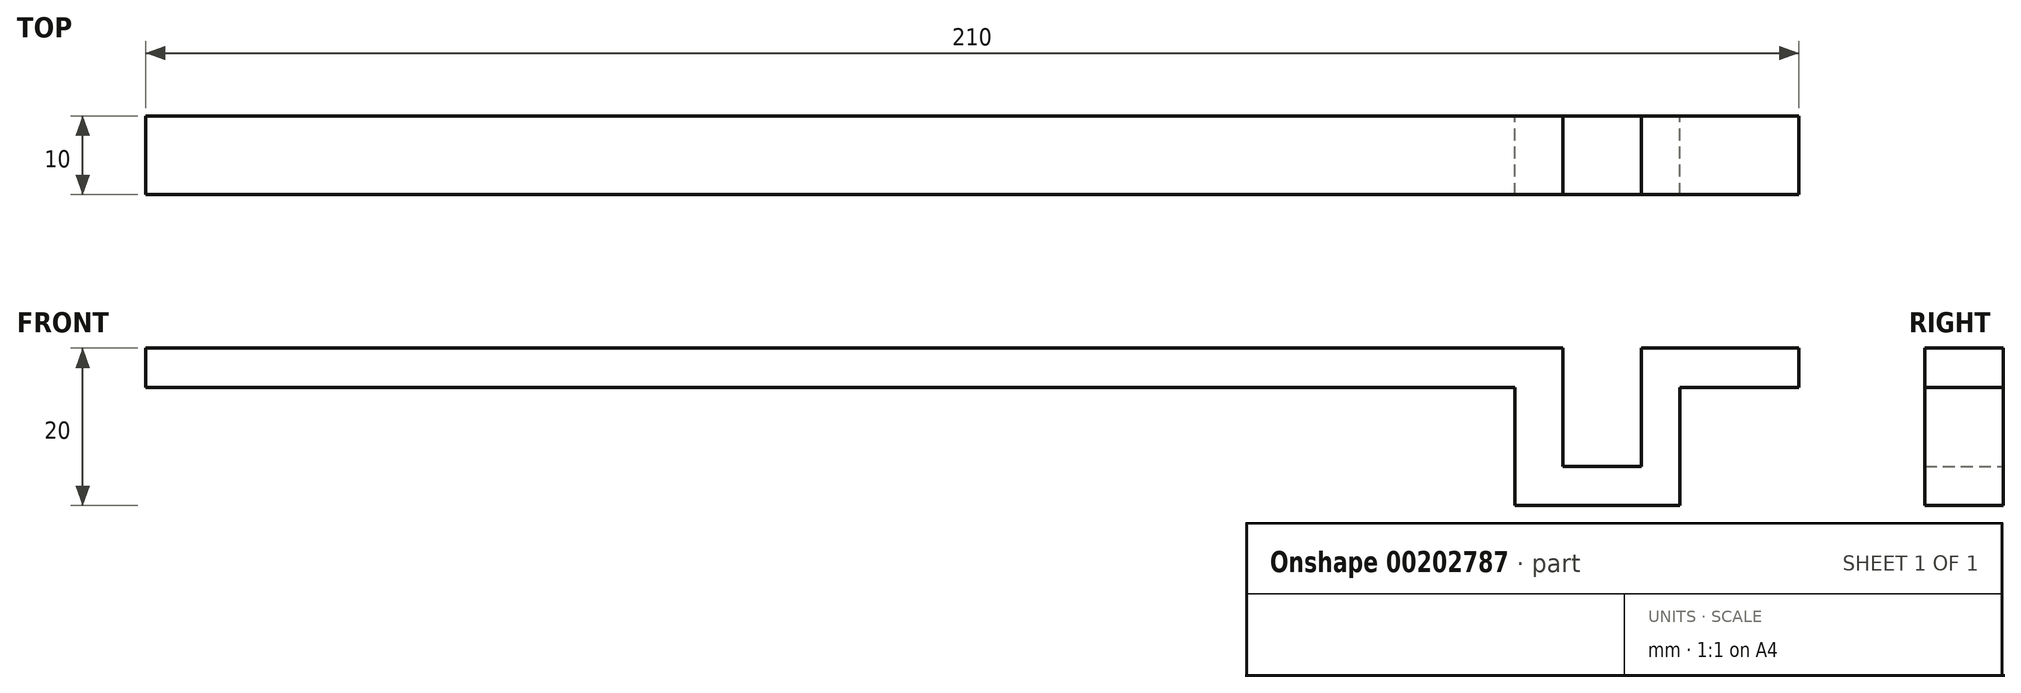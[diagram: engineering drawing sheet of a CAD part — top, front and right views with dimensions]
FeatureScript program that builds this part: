
annotation { "Feature Type Name" : "Feature", "Feature Type Description" : "" }
export const myFeature = defineFeature(function(context is Context, id is Id, definition is map)
    precondition{}
    {
        {
            var Q0;
            Q0=qCreatedBy(makeId("Front.planeOp"),FACE);
            var sketch = newSketch(context, id + "F0", { "sketchPlane" : qUnion([Q0])});
            skLineSegment(sketch, "E0", {"start": v(0, 0) * mm, "end": v(180, 0) * mm});
            skLineSegment(sketch, "E1", {"start": v(180, 0) * mm, "end": v(180, -15) * mm});
            skLineSegment(sketch, "E2", {"start": v(180, -15) * mm, "end": v(190, -15) * mm});
            skLineSegment(sketch, "E3", {"start": v(190, -15) * mm, "end": v(190, 0) * mm});
            skLineSegment(sketch, "E4", {"start": v(190, 0) * mm, "end": v(210, 0) * mm});
            skLineSegment(sketch, "E5", {"start": v(0, 0) * mm, "end": v(0, -5) * mm});
            skLineSegment(sketch, "E6", {"start": v(0, -5) * mm, "end": v(173.92, -5) * mm});
            skLineSegment(sketch, "E7", {"start": v(173.92, -5) * mm, "end": v(173.92, -20) * mm});
            skLineSegment(sketch, "E8", {"start": v(173.92, -20) * mm, "end": v(194.9, -20) * mm});
            skLineSegment(sketch, "E9", {"start": v(194.9, -20) * mm, "end": v(194.9, -5) * mm});
            skLineSegment(sketch, "E10", {"start": v(210, 0) * mm, "end": v(210, -5) * mm});
            skLineSegment(sketch, "E11", {"start": v(210, -5) * mm, "end": v(194.9, -5) * mm});
            skSolve(sketch);
        }
        {
            var Q0;
            Q0 = qSketchRegion(id + "F0", true);
            extrude(context, id + "F1", {"entities" : qUnion([Q0]), "depth" : 10 * mm});
        }
    });
